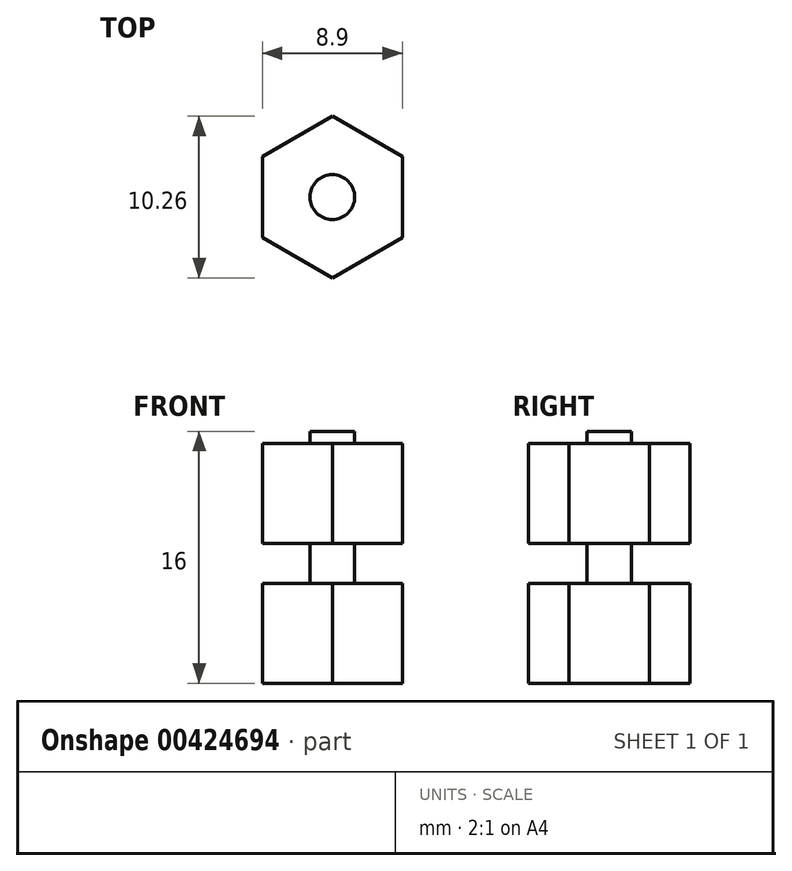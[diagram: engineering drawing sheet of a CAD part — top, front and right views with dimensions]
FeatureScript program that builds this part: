
annotation { "Feature Type Name" : "Feature", "Feature Type Description" : "" }
export const myFeature = defineFeature(function(context is Context, id is Id, definition is map)
    precondition{}
    {
        {
            var Q0;
            Q0=qCreatedBy(makeId("Top.planeOp"),FACE);
            var sketch = newSketch(context, id + "F0", { "sketchPlane" : qUnion([Q0])});
            skCircle(sketch, "E0.cCircle", {"center": v(0, 0) * mm, "radius": 4.45 * mm, "construction": true});
            skLineSegment(sketch, "E0.0", {"start": v(4.45, 2.57) * mm, "end": v(4.45, -2.57) * mm});
            skLineSegment(sketch, "E0.1", {"start": v(4.45, -2.57) * mm, "end": v(0, -5.13) * mm});
            skLineSegment(sketch, "E0.2", {"start": v(0, -5.13) * mm, "end": v(-4.44, -2.57) * mm});
            skLineSegment(sketch, "E0.3", {"start": v(-4.44, -2.57) * mm, "end": v(-4.45, 2.57) * mm});
            skLineSegment(sketch, "E0.4", {"start": v(-4.44, 2.57) * mm, "end": v(0, 5.13) * mm});
            skLineSegment(sketch, "E0.5", {"start": v(0, 5.13) * mm, "end": v(4.44, 2.57) * mm});
            skPoint(sketch, "E0.0.midPoint", {"position": v(4.45, 0) * mm});
            skCircle(sketch, "E1", {"center": v(0, 0) * mm, "radius": 1.42 * mm});
            skSolve(sketch);
        }
        {
            var Q0;
            Q0=makeQuery(id+"F0.imprint","IMPRINT",FACE,{"disambiguationData":[TD([[makeQuery(id+"F0.imprint","IMPRINT",EDGE,{"derivedFrom":sQuery(id+"F0.wireOp",EDGE,"E0.0")}),-1.0]])]});
            extrude(context, id + "F1", {"entities" : qUnion([Q0]), "oppositeDirection" : true, "depth" : 6.35 * mm});
        }
        {
            var Q0;
            Q0=makeQuery(id+"F0.imprint","IMPRINT",FACE,{"disambiguationData":[TD([[makeQuery(id+"F0.imprint","IMPRINT",EDGE,{"derivedFrom":sQuery(id+"F0.wireOp",EDGE,"E1")}),1.0]])]});
            extrude(context, id + "F2", {"entities" : qUnion([Q0]), "operationType" : NewBodyOperationType.ADD, "depth" : 0.76 * mm, "hasSecondDirection" : true, "secondDirectionOppositeDirection" : true, "secondDirectionDepth" : 15.24 * mm});
        }
        {
            var Q0;
            Q0=makeQuery(id+"F0.imprint","IMPRINT",FACE,{"disambiguationData":[TD([[makeQuery(id+"F0.imprint","IMPRINT",EDGE,{"derivedFrom":sQuery(id+"F0.wireOp",EDGE,"E0.0")}),-1.0]])]});
            extrude(context, id + "F3", {"entities" : qUnion([Q0]), "operationType" : NewBodyOperationType.ADD, "oppositeDirection" : true, "depth" : 15.24 * mm, "hasSecondDirection" : true, "secondDirectionOppositeDirection" : true, "secondDirectionDepth" : 8.9 * mm});
        }
    });
